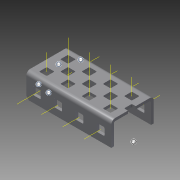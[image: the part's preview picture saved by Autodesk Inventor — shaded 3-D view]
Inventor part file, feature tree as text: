
AUTODESK INVENTOR PART (.ipt)
format: ipt  version: 2015 (Build 190159000, 159)  size: 1,923,584 bytes
history: native  units: in
note: dims shown in document units (in); Inventor stores cm internally (conversion verified against a paired STEP export)
features: other x26, pattern_linear x3, sheet_metal_op x1, extrude x1, imported_body x1, sketch x1
ambient origin geometry x8: Origin, YZ Plane, XZ Plane, XY Plane, X Axis, Y Axis, Z Axis, Center Point
bodies: Body1 (feature_tree)
feature tree (33):
  sheet_metal_op  "Fold1"
  other  "C-Channel"
  extrude  "length cut"  Depth=0.5in
  other  "top axis"
  other  "inner axis"
  other  "front axis"
  other  "back axis"
  pattern_linear  "top axes"  Spacing1=0.5in  [1 undecoded]
  pattern_linear  "inner axes"  Spacing1=0.5in  [1 undecoded]
  pattern_linear  "horiz axes"  Spacing1=-2.0in  [1 undecoded]
  other  "right plane"
  imported_body  "Base1"
  sketch  "Sketch1"  dims[d1=0.0in d4=0.5in d5=0.7874in d7=0.5in d10=0.5in d13=0.5in d14=-2.0in d15=0.0in d16=0.0in d17=0.0in d18=0.0in d19=0.0in]
  other  "Work Point1"
  other  "Work Point2"
  other  "Work Point3"
  other  "Work Point4"
  other  "Work Axis5"
  other  "Work Axis6"
  other  "Work Axis7"
  other  "Work Axis11"
  other  "Work Axis12"
  other  "Work Axis13"
  other  "Work Axis14"
  other  "Work Axis18"
  other  "Work Axis19"
  other  "Work Axis23"
  other  "Work Axis24"
  other  "Work Axis25"
  other  "Work Axis30"
  other  "Work Axis31"
  other  "Work Axis32"
  other  "left plane"
note: 3 required parameter values undecoded (feature->parameter linkage not recoverable at this tier; creation-order binding heuristic only, values carry confidence <= 0.55)
